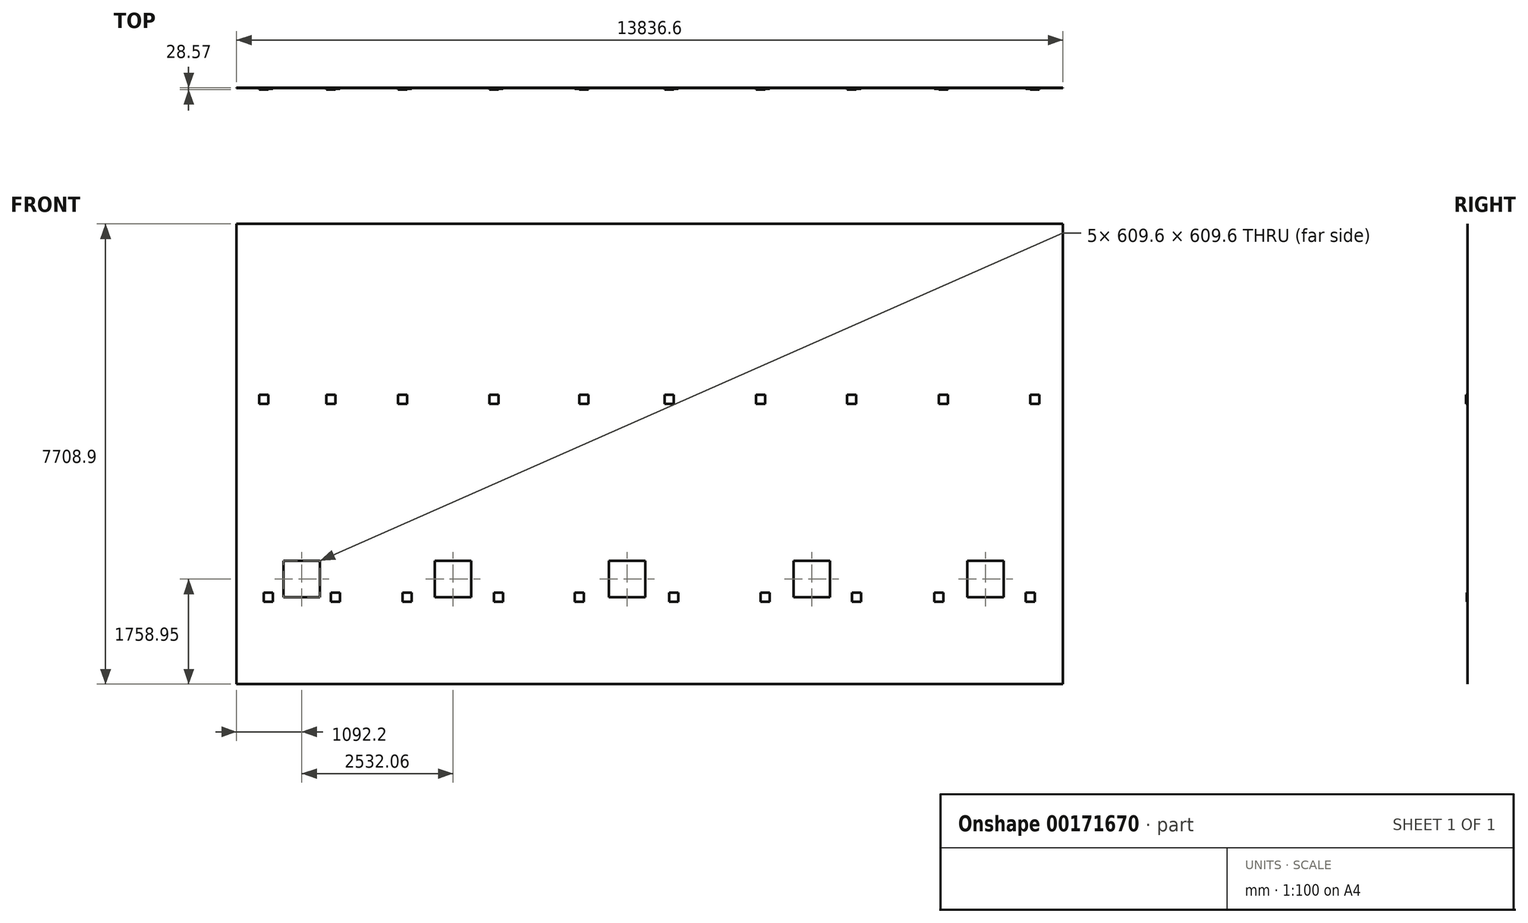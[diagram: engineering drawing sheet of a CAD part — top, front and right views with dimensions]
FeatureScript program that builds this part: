
annotation { "Feature Type Name" : "Feature", "Feature Type Description" : "" }
export const myFeature = defineFeature(function(context is Context, id is Id, definition is map)
    precondition{}
    {
        {
            var Q0;
            Q0=qCreatedBy(makeId("Front.planeOp"),FACE);
            var sketch = newSketch(context, id + "F0", { "sketchPlane" : qUnion([Q0])});
            skLineSegment(sketch, "E0.bottom", {"start": v(0, 0) * mm, "end": v(13836.65, 0) * mm});
            skLineSegment(sketch, "E0.top", {"start": v(0, 7708.9) * mm, "end": v(13836.65, 7708.9) * mm});
            skLineSegment(sketch, "E0.left", {"start": v(0, 0) * mm, "end": v(0, 7708.9) * mm});
            skLineSegment(sketch, "E0.right", {"start": v(13836.65, 0) * mm, "end": v(13836.65, 7708.9) * mm});
            skSolve(sketch);
        }
        {
            var Q0;
            Q0 = qSketchRegion(id + "F0", true);
            extrude(context, id + "F1", {"entities" : qUnion([Q0]), "depth" : 3.17 * mm});
        }
        {
            var Q0;
            Q0=makeQuery(id+"F1.opExtrude","CAP_FACE",FACE,{"disambiguationData":[OSD([sQuery(id+"F0.wireOp",EDGE,"E0.bottom"),sQuery(id+"F0.wireOp",EDGE,"E0.top"),sQuery(id+"F0.wireOp",EDGE,"E0.left"),sQuery(id+"F0.wireOp",EDGE,"E0.right")])],"isStart":false});
            var sketch = newSketch(context, id + "F2", { "sketchPlane" : qUnion([Q0])});
            skLineSegment(sketch, "E1.bottom", {"start": v(787.4, 2063.75) * mm, "end": v(1397, 2063.75) * mm});
            skLineSegment(sketch, "E1.top", {"start": v(787.4, 1454.15) * mm, "end": v(1397, 1454.15) * mm});
            skLineSegment(sketch, "E1.left", {"start": v(787.4, 2063.75) * mm, "end": v(787.4, 1454.15) * mm});
            skLineSegment(sketch, "E1.right", {"start": v(1397, 2063.75) * mm, "end": v(1397, 1454.15) * mm});
            skLineSegment(sketch, "E2.bottom", {"start": v(3319.46, 1454.15) * mm, "end": v(3929.06, 1454.15) * mm});
            skLineSegment(sketch, "E2.top", {"start": v(3319.46, 2063.75) * mm, "end": v(3929.06, 2063.75) * mm});
            skLineSegment(sketch, "E2.left", {"start": v(3319.46, 1454.15) * mm, "end": v(3319.46, 2063.75) * mm});
            skLineSegment(sketch, "E2.right", {"start": v(3929.06, 1454.15) * mm, "end": v(3929.06, 2063.75) * mm});
            skLineSegment(sketch, "E3.bottom", {"start": v(6232.53, 2063.75) * mm, "end": v(6842.13, 2063.75) * mm});
            skLineSegment(sketch, "E3.top", {"start": v(6232.53, 1454.15) * mm, "end": v(6842.13, 1454.15) * mm});
            skLineSegment(sketch, "E3.left", {"start": v(6232.53, 2063.75) * mm, "end": v(6232.53, 1454.15) * mm});
            skLineSegment(sketch, "E3.right", {"start": v(6842.13, 2063.75) * mm, "end": v(6842.13, 1454.15) * mm});
            skLineSegment(sketch, "E4.bottom", {"start": v(9323.39, 1454.15) * mm, "end": v(9932.99, 1454.15) * mm});
            skLineSegment(sketch, "E4.top", {"start": v(9323.39, 2063.75) * mm, "end": v(9932.99, 2063.75) * mm});
            skLineSegment(sketch, "E4.left", {"start": v(9323.39, 1454.15) * mm, "end": v(9323.39, 2063.75) * mm});
            skLineSegment(sketch, "E4.right", {"start": v(9932.99, 1454.15) * mm, "end": v(9932.99, 2063.75) * mm});
            skLineSegment(sketch, "E5.bottom", {"start": v(12236.45, 1454.15) * mm, "end": v(12846.05, 1454.15) * mm});
            skLineSegment(sketch, "E5.top", {"start": v(12236.45, 2063.75) * mm, "end": v(12846.05, 2063.75) * mm});
            skLineSegment(sketch, "E5.left", {"start": v(12236.45, 1454.15) * mm, "end": v(12236.45, 2063.75) * mm});
            skLineSegment(sketch, "E5.right", {"start": v(12846.05, 1454.15) * mm, "end": v(12846.05, 2063.75) * mm});
            skSolve(sketch);
        }
        {
            var Q0;
            Q0 = qSketchRegion(id + "F2", true);
            extrude(context, id + "F3", {"entities" : qUnion([Q0]), "operationType" : NewBodyOperationType.REMOVE, "endBound" : BoundingType.THROUGH_ALL, "oppositeDirection" : true, "depth" : 25.4 * mm});
        }
        {
            var Q0;
            Q0=makeQuery(id+"F1.opExtrude","CAP_FACE",FACE,{"disambiguationData":[OSD([sQuery(id+"F0.wireOp",EDGE,"E0.bottom"),sQuery(id+"F0.wireOp",EDGE,"E0.top"),sQuery(id+"F0.wireOp",EDGE,"E0.left"),sQuery(id+"F0.wireOp",EDGE,"E0.right")])],"isStart":false});
            var sketch = newSketch(context, id + "F4", { "sketchPlane" : qUnion([Q0])});
            skLineSegment(sketch, "E6.bottom", {"start": v(457.2, 1530.35) * mm, "end": v(609.6, 1530.35) * mm});
            skLineSegment(sketch, "E6.top", {"start": v(457.2, 1377.95) * mm, "end": v(609.6, 1377.95) * mm});
            skLineSegment(sketch, "E6.left", {"start": v(457.2, 1530.35) * mm, "end": v(457.2, 1377.95) * mm});
            skLineSegment(sketch, "E6.right", {"start": v(609.6, 1530.35) * mm, "end": v(609.6, 1377.95) * mm});
            skLineSegment(sketch, "E7.bottom", {"start": v(1581.15, 1530.35) * mm, "end": v(1733.55, 1530.35) * mm});
            skLineSegment(sketch, "E7.top", {"start": v(1581.15, 1377.95) * mm, "end": v(1733.55, 1377.95) * mm});
            skLineSegment(sketch, "E7.left", {"start": v(1581.15, 1530.35) * mm, "end": v(1581.15, 1377.95) * mm});
            skLineSegment(sketch, "E7.right", {"start": v(1733.55, 1530.35) * mm, "end": v(1733.55, 1377.95) * mm});
            skLineSegment(sketch, "E8.bottom", {"start": v(2781.3, 1530.35) * mm, "end": v(2933.7, 1530.35) * mm});
            skLineSegment(sketch, "E8.top", {"start": v(2781.3, 1377.95) * mm, "end": v(2933.7, 1377.95) * mm});
            skLineSegment(sketch, "E8.left", {"start": v(2781.3, 1530.35) * mm, "end": v(2781.3, 1377.95) * mm});
            skLineSegment(sketch, "E8.right", {"start": v(2933.7, 1530.35) * mm, "end": v(2933.7, 1377.95) * mm});
            skLineSegment(sketch, "E9.bottom", {"start": v(4311.65, 1530.35) * mm, "end": v(4464.05, 1530.35) * mm});
            skLineSegment(sketch, "E9.top", {"start": v(4311.65, 1377.95) * mm, "end": v(4464.05, 1377.95) * mm});
            skLineSegment(sketch, "E9.left", {"start": v(4311.65, 1530.35) * mm, "end": v(4311.65, 1377.95) * mm});
            skLineSegment(sketch, "E9.right", {"start": v(4464.05, 1530.35) * mm, "end": v(4464.05, 1377.95) * mm});
            skLineSegment(sketch, "E10.bottom", {"start": v(5664.2, 1530.35) * mm, "end": v(5816.6, 1530.35) * mm});
            skLineSegment(sketch, "E10.top", {"start": v(5664.2, 1377.95) * mm, "end": v(5816.6, 1377.95) * mm});
            skLineSegment(sketch, "E10.left", {"start": v(5664.2, 1530.35) * mm, "end": v(5664.2, 1377.95) * mm});
            skLineSegment(sketch, "E10.right", {"start": v(5816.6, 1530.35) * mm, "end": v(5816.6, 1377.95) * mm});
            skLineSegment(sketch, "E11.bottom", {"start": v(7245.35, 1530.35) * mm, "end": v(7397.75, 1530.35) * mm});
            skLineSegment(sketch, "E11.top", {"start": v(7245.35, 1377.95) * mm, "end": v(7397.75, 1377.95) * mm});
            skLineSegment(sketch, "E11.left", {"start": v(7245.35, 1530.35) * mm, "end": v(7245.35, 1377.95) * mm});
            skLineSegment(sketch, "E11.right", {"start": v(7397.75, 1530.35) * mm, "end": v(7397.75, 1377.95) * mm});
            skPoint(sketch, "E12.firstSnap0", {"position": v(7321.55, 1530.35) * mm});
            skLineSegment(sketch, "E12.bottom", {"start": v(8775.7, 1530.35) * mm, "end": v(8928.1, 1530.35) * mm});
            skLineSegment(sketch, "E12.top", {"start": v(8775.7, 1377.95) * mm, "end": v(8928.1, 1377.95) * mm});
            skLineSegment(sketch, "E12.left", {"start": v(8775.7, 1530.35) * mm, "end": v(8775.7, 1377.95) * mm});
            skLineSegment(sketch, "E12.right", {"start": v(8928.1, 1530.35) * mm, "end": v(8928.1, 1377.95) * mm});
            skLineSegment(sketch, "E13.bottom", {"start": v(10306.05, 1530.35) * mm, "end": v(10458.45, 1530.35) * mm});
            skLineSegment(sketch, "E13.top", {"start": v(10306.05, 1377.95) * mm, "end": v(10458.45, 1377.95) * mm});
            skLineSegment(sketch, "E13.left", {"start": v(10306.05, 1530.35) * mm, "end": v(10306.05, 1377.95) * mm});
            skLineSegment(sketch, "E13.right", {"start": v(10458.45, 1530.35) * mm, "end": v(10458.45, 1377.95) * mm});
            skLineSegment(sketch, "E14.bottom", {"start": v(11684, 1530.35) * mm, "end": v(11836.4, 1530.35) * mm});
            skLineSegment(sketch, "E14.top", {"start": v(11684, 1377.95) * mm, "end": v(11836.4, 1377.95) * mm});
            skLineSegment(sketch, "E14.left", {"start": v(11684, 1530.35) * mm, "end": v(11684, 1377.95) * mm});
            skLineSegment(sketch, "E14.right", {"start": v(11836.4, 1530.35) * mm, "end": v(11836.4, 1377.95) * mm});
            skLineSegment(sketch, "E15.bottom", {"start": v(13214.35, 1530.35) * mm, "end": v(13366.75, 1530.35) * mm});
            skLineSegment(sketch, "E15.top", {"start": v(13214.35, 1377.95) * mm, "end": v(13366.75, 1377.95) * mm});
            skLineSegment(sketch, "E15.left", {"start": v(13214.35, 1530.35) * mm, "end": v(13214.35, 1377.95) * mm});
            skLineSegment(sketch, "E15.right", {"start": v(13366.75, 1530.35) * mm, "end": v(13366.75, 1377.95) * mm});
            skSolve(sketch);
        }
        {
            var Q0;
            Q0 = qSketchRegion(id + "F4", true);
            extrude(context, id + "F5", {"entities" : qUnion([Q0]), "operationType" : NewBodyOperationType.ADD, "depth" : 6.35 * mm});
        }
        {
            var Q0;
            Q0 = qSketchRegion(id + "F4", true);
            extrude(context, id + "F6", {"entities" : qUnion([Q0]), "operationType" : NewBodyOperationType.ADD, "depth" : 12.7 * mm});
        }
        {
            var Q0;
            Q0=makeQuery(id+"F1.opExtrude","CAP_FACE",FACE,{"disambiguationData":[OSD([sQuery(id+"F0.wireOp",EDGE,"E0.bottom"),sQuery(id+"F0.wireOp",EDGE,"E0.top"),sQuery(id+"F0.wireOp",EDGE,"E0.left"),sQuery(id+"F0.wireOp",EDGE,"E0.right")])],"isStart":false});
            var sketch = newSketch(context, id + "F7", { "sketchPlane" : qUnion([Q0])});
            skLineSegment(sketch, "E16.bottom", {"start": v(381, 4845.05) * mm, "end": v(533.4, 4845.05) * mm});
            skLineSegment(sketch, "E16.top", {"start": v(381, 4692.65) * mm, "end": v(533.4, 4692.65) * mm});
            skLineSegment(sketch, "E16.left", {"start": v(381, 4845.05) * mm, "end": v(381, 4692.65) * mm});
            skLineSegment(sketch, "E16.right", {"start": v(533.4, 4845.05) * mm, "end": v(533.4, 4692.65) * mm});
            skLineSegment(sketch, "E17.bottom", {"start": v(1504.95, 4845.05) * mm, "end": v(1657.35, 4845.05) * mm});
            skLineSegment(sketch, "E17.top", {"start": v(1504.95, 4692.65) * mm, "end": v(1657.35, 4692.65) * mm});
            skLineSegment(sketch, "E17.left", {"start": v(1504.95, 4845.05) * mm, "end": v(1504.95, 4692.65) * mm});
            skLineSegment(sketch, "E17.right", {"start": v(1657.35, 4845.05) * mm, "end": v(1657.35, 4692.65) * mm});
            skLineSegment(sketch, "E18.bottom", {"start": v(2705.1, 4845.05) * mm, "end": v(2857.5, 4845.05) * mm});
            skLineSegment(sketch, "E18.top", {"start": v(2705.1, 4692.65) * mm, "end": v(2857.5, 4692.65) * mm});
            skLineSegment(sketch, "E18.left", {"start": v(2705.1, 4845.05) * mm, "end": v(2705.1, 4692.65) * mm});
            skLineSegment(sketch, "E18.right", {"start": v(2857.5, 4845.05) * mm, "end": v(2857.5, 4692.65) * mm});
            skLineSegment(sketch, "E19.bottom", {"start": v(4235.45, 4845.05) * mm, "end": v(4387.85, 4845.05) * mm});
            skLineSegment(sketch, "E19.top", {"start": v(4235.45, 4692.65) * mm, "end": v(4387.85, 4692.65) * mm});
            skLineSegment(sketch, "E19.left", {"start": v(4235.45, 4845.05) * mm, "end": v(4235.45, 4692.65) * mm});
            skLineSegment(sketch, "E19.right", {"start": v(4387.85, 4845.05) * mm, "end": v(4387.85, 4692.65) * mm});
            skLineSegment(sketch, "E20.bottom", {"start": v(5740.4, 4845.05) * mm, "end": v(5892.8, 4845.05) * mm});
            skLineSegment(sketch, "E20.top", {"start": v(5740.4, 4692.65) * mm, "end": v(5892.8, 4692.65) * mm});
            skLineSegment(sketch, "E20.left", {"start": v(5740.4, 4845.05) * mm, "end": v(5740.4, 4692.65) * mm});
            skLineSegment(sketch, "E20.right", {"start": v(5892.8, 4845.05) * mm, "end": v(5892.8, 4692.65) * mm});
            skLineSegment(sketch, "E21.bottom", {"start": v(7169.15, 4845.05) * mm, "end": v(7321.55, 4845.05) * mm});
            skLineSegment(sketch, "E21.top", {"start": v(7169.15, 4692.65) * mm, "end": v(7321.55, 4692.65) * mm});
            skLineSegment(sketch, "E21.left", {"start": v(7169.15, 4845.05) * mm, "end": v(7169.15, 4692.65) * mm});
            skLineSegment(sketch, "E21.right", {"start": v(7321.55, 4845.05) * mm, "end": v(7321.55, 4692.65) * mm});
            skLineSegment(sketch, "E22.bottom", {"start": v(8699.5, 4845.05) * mm, "end": v(8851.9, 4845.05) * mm});
            skLineSegment(sketch, "E22.top", {"start": v(8699.5, 4692.65) * mm, "end": v(8851.9, 4692.65) * mm});
            skLineSegment(sketch, "E22.left", {"start": v(8699.5, 4845.05) * mm, "end": v(8699.5, 4692.65) * mm});
            skLineSegment(sketch, "E22.right", {"start": v(8851.9, 4845.05) * mm, "end": v(8851.9, 4692.65) * mm});
            skLineSegment(sketch, "E23.bottom", {"start": v(10223.5, 4845.05) * mm, "end": v(10375.9, 4845.05) * mm});
            skLineSegment(sketch, "E23.top", {"start": v(10223.5, 4692.65) * mm, "end": v(10375.9, 4692.65) * mm});
            skLineSegment(sketch, "E23.left", {"start": v(10223.5, 4845.05) * mm, "end": v(10223.5, 4692.65) * mm});
            skLineSegment(sketch, "E23.right", {"start": v(10375.9, 4845.05) * mm, "end": v(10375.9, 4692.65) * mm});
            skLineSegment(sketch, "E24.bottom", {"start": v(11760.2, 4845.05) * mm, "end": v(11912.6, 4845.05) * mm});
            skLineSegment(sketch, "E24.top", {"start": v(11760.2, 4692.65) * mm, "end": v(11912.6, 4692.65) * mm});
            skLineSegment(sketch, "E24.left", {"start": v(11760.2, 4845.05) * mm, "end": v(11760.2, 4692.65) * mm});
            skLineSegment(sketch, "E24.right", {"start": v(11912.6, 4845.05) * mm, "end": v(11912.6, 4692.65) * mm});
            skLineSegment(sketch, "E25.bottom", {"start": v(13290.55, 4845.05) * mm, "end": v(13442.95, 4845.05) * mm});
            skLineSegment(sketch, "E25.top", {"start": v(13290.55, 4692.65) * mm, "end": v(13442.95, 4692.65) * mm});
            skLineSegment(sketch, "E25.left", {"start": v(13290.55, 4845.05) * mm, "end": v(13290.55, 4692.65) * mm});
            skLineSegment(sketch, "E25.right", {"start": v(13442.95, 4845.05) * mm, "end": v(13442.95, 4692.65) * mm});
            skSolve(sketch);
        }
        {
            var Q0;
            Q0 = qSketchRegion(id + "F7", true);
            extrude(context, id + "F8", {"entities" : qUnion([Q0]), "operationType" : NewBodyOperationType.ADD, "depth" : 25.4 * mm});
        }
    });
